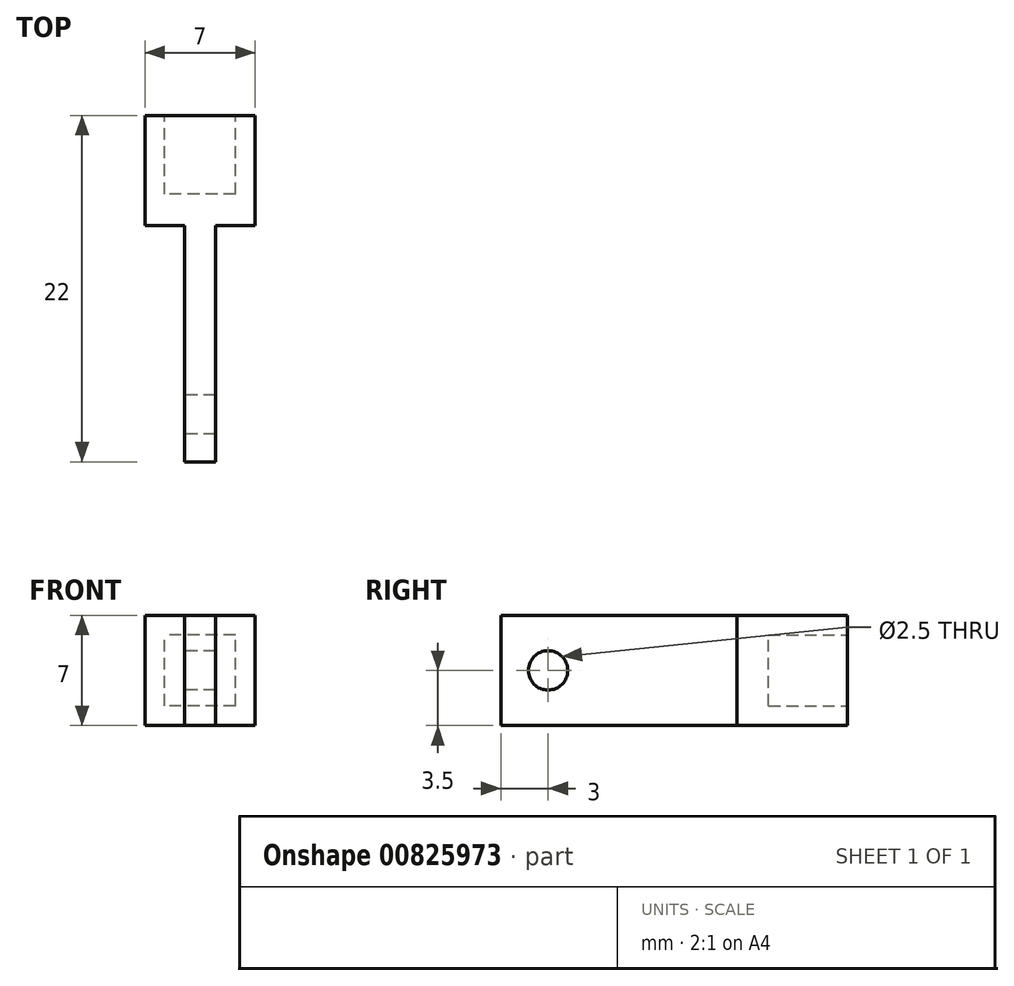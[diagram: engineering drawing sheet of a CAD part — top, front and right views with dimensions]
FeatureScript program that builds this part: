
annotation { "Feature Type Name" : "Feature", "Feature Type Description" : "" }
export const myFeature = defineFeature(function(context is Context, id is Id, definition is map)
    precondition{}
    {
        {
            var Q0;
            Q0=qCreatedBy(makeId("Front.planeOp"),FACE);
            var sketch = newSketch(context, id + "F0", { "sketchPlane" : qUnion([Q0])});
            skPoint(sketch, "E0.middle", {"position": v(0, 0) * mm});
            skLineSegment(sketch, "E1.bottom", {"start": v(2.25, -2.25) * mm, "end": v(-2.25, -2.25) * mm});
            skLineSegment(sketch, "E1.top", {"start": v(2.25, 2.25) * mm, "end": v(-2.25, 2.25) * mm});
            skLineSegment(sketch, "E1.left", {"start": v(2.25, -2.25) * mm, "end": v(2.25, 2.25) * mm});
            skLineSegment(sketch, "E1.right", {"start": v(-2.25, -2.25) * mm, "end": v(-2.25, 2.25) * mm});
            skLineSegment(sketch, "E2.bottom", {"start": v(-3.5, 3.5) * mm, "end": v(3.5, 3.5) * mm});
            skLineSegment(sketch, "E2.top", {"start": v(-3.5, -3.5) * mm, "end": v(3.5, -3.5) * mm});
            skLineSegment(sketch, "E2.left", {"start": v(-3.5, 3.5) * mm, "end": v(-3.5, -3.5) * mm});
            skLineSegment(sketch, "E2.right", {"start": v(3.5, 3.5) * mm, "end": v(3.5, -3.5) * mm});
            skSolve(sketch);
        }
        {
            var Q0;
            Q0=makeQuery(id+"F0.imprint","IMPRINT",FACE,{"disambiguationData":[TD([[makeQuery(id+"F0.imprint","IMPRINT",EDGE,{"derivedFrom":sQuery(id+"F0.wireOp",EDGE,"E1.bottom")}),1.0]])]});
            extrude(context, id + "F1", {"entities" : qUnion([Q0]), "depth" : 5 * mm, "offsetDistance" : 25 * mm});
        }
        {
            var Q0;
            Q0=makeQuery(id+"F1.opExtrude","CAP_FACE",FACE,{"disambiguationData":[OSD([sQuery(id+"F0.wireOp",EDGE,"E1.bottom"),sQuery(id+"F0.wireOp",EDGE,"E1.top"),sQuery(id+"F0.wireOp",EDGE,"E1.left"),sQuery(id+"F0.wireOp",EDGE,"E1.right"),sQuery(id+"F0.wireOp",EDGE,"E2.bottom"),sQuery(id+"F0.wireOp",EDGE,"E2.top"),sQuery(id+"F0.wireOp",EDGE,"E2.left"),sQuery(id+"F0.wireOp",EDGE,"E2.right")])],"isStart":false});
            var sketch = newSketch(context, id + "F2", { "sketchPlane" : qUnion([Q0])});
            skLineSegment(sketch, "E3.bottom", {"start": v(3.5, 3.5) * mm, "end": v(-3.5, 3.5) * mm});
            skLineSegment(sketch, "E3.top", {"start": v(3.5, -3.5) * mm, "end": v(-3.5, -3.5) * mm});
            skLineSegment(sketch, "E3.left", {"start": v(3.5, 3.5) * mm, "end": v(3.5, -3.5) * mm});
            skLineSegment(sketch, "E3.right", {"start": v(-3.5, 3.5) * mm, "end": v(-3.5, -3.5) * mm});
            skPoint(sketch, "E3.middle", {"position": v(0, 0) * mm});
            skSolve(sketch);
        }
        {
            var Q0;
            Q0 = qSketchRegion(id + "F2", true);
            extrude(context, id + "F3", {"entities" : qUnion([Q0]), "operationType" : NewBodyOperationType.ADD, "depth" : 2 * mm, "offsetDistance" : 25 * mm});
        }
        {
            var Q0;
            Q0=makeQuery(id+"F3.opExtrude","CAP_FACE",FACE,{"disambiguationData":[OSD([sQuery(id+"F2.wireOp",EDGE,"E3.bottom"),sQuery(id+"F2.wireOp",EDGE,"E3.top"),sQuery(id+"F2.wireOp",EDGE,"E3.left"),sQuery(id+"F2.wireOp",EDGE,"E3.right")])],"isStart":false});
            var sketch = newSketch(context, id + "F4", { "sketchPlane" : qUnion([Q0])});
            skLineSegment(sketch, "E4.bottom", {"start": v(0.98, -3.5) * mm, "end": v(-0.98, -3.5) * mm});
            skLineSegment(sketch, "E4.top", {"start": v(0.98, 3.5) * mm, "end": v(-0.98, 3.5) * mm});
            skLineSegment(sketch, "E4.left", {"start": v(0.98, -3.5) * mm, "end": v(0.98, 3.5) * mm});
            skLineSegment(sketch, "E4.right", {"start": v(-0.98, -3.5) * mm, "end": v(-0.98, 3.5) * mm});
            skPoint(sketch, "E4.middle", {"position": v(0, 0) * mm});
            skSolve(sketch);
        }
        {
            var Q0;
            Q0 = qSketchRegion(id + "F4", true);
            var Q1;
            Q1=makeQuery(id+"F4.imprint","IMPRINT",FACE,{"disambiguationData":[TD([[makeQuery(id+"F4.imprint","IMPRINT",EDGE,{"derivedFrom":sQuery(id+"F4.wireOp",EDGE,"E4.bottom")}),1.0]])]});
            extrude(context, id + "F5", {"entities" : qUnion([Q0, Q1]), "operationType" : NewBodyOperationType.ADD, "depth" : 15 * mm, "offsetDistance" : 25 * mm});
        }
        {
            var Q0;
            Q0=makeQuery(id+"F5.opExtrude","SWEPT_FACE",FACE,{"disambiguationData":[OSD([sQuery(id+"F4.wireOp",EDGE,"E4.right")])]});
            var sketch = newSketch(context, id + "F6", { "sketchPlane" : qUnion([Q0])});
            skCircle(sketch, "E5", {"center": v(19, 0) * mm, "radius": 1.25 * mm});
            skSolve(sketch);
        }
        {
            var Q0;
            Q0=makeQuery(id+"F6.imprint","IMPRINT",FACE,{"disambiguationData":[TD([[makeQuery(id+"F6.imprint","IMPRINT",EDGE,{"derivedFrom":sQuery(id+"F6.wireOp",EDGE,"E5")}),1.0]])]});
            extrude(context, id + "F7", {"entities" : qUnion([Q0]), "operationType" : NewBodyOperationType.REMOVE, "oppositeDirection" : true, "depth" : 25 * mm, "offsetDistance" : 25 * mm});
        }
    });
